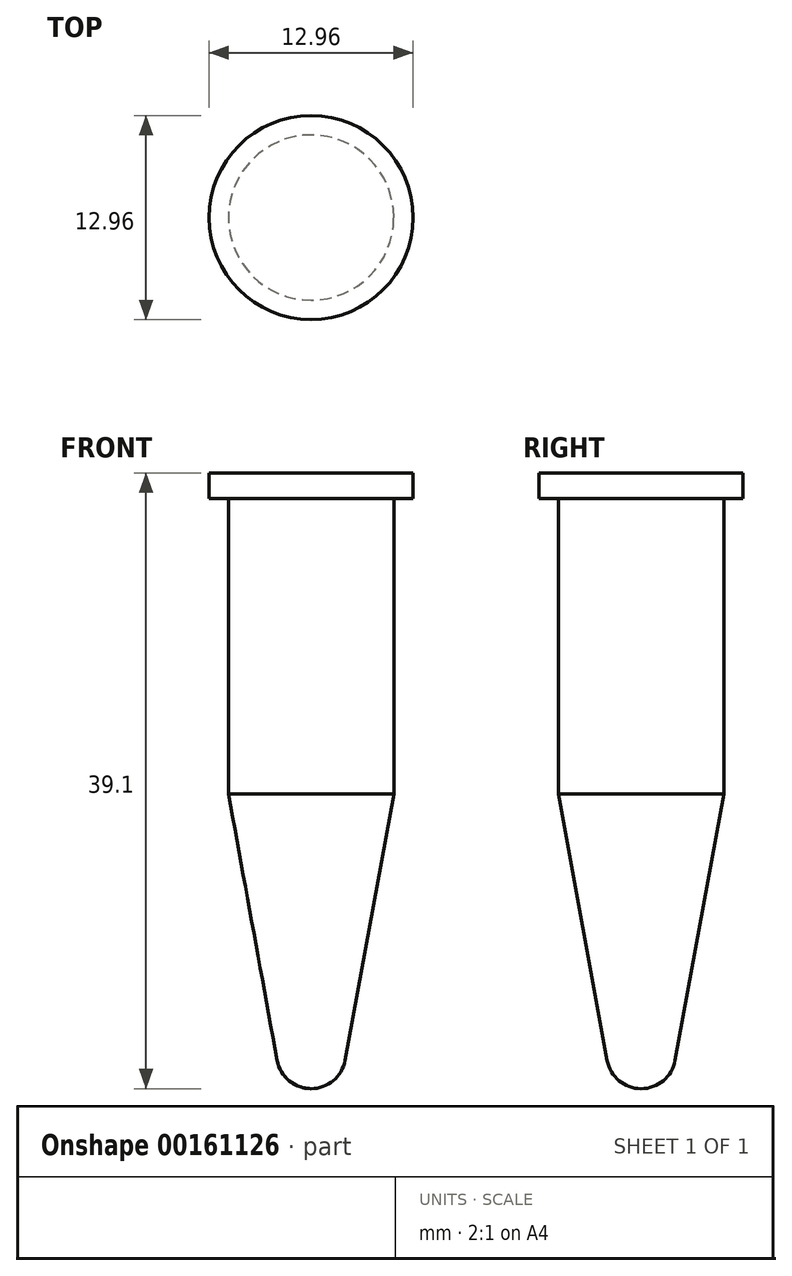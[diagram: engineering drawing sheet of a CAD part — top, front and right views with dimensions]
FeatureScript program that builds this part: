
annotation { "Feature Type Name" : "Feature", "Feature Type Description" : "" }
export const myFeature = defineFeature(function(context is Context, id is Id, definition is map)
    precondition{}
    {
        {
            var Q0;
            Q0=qCreatedBy(makeId("Front.planeOp"),FACE);
            var sketch = newSketch(context, id + "F0", { "sketchPlane" : qUnion([Q0])});
            skLineSegment(sketch, "E0", {"start": v(0, 0) * mm, "end": v(0, 39.1) * mm});
            skLineSegment(sketch, "E1", {"start": v(5.25, 37.5) * mm, "end": v(5.25, 18.72) * mm});
            skArc(sketch, "E2", {"start": v(0, 0) * mm, "mid": v(1.4, 0.5) * mm, "end": v(2.16, 1.8) * mm});
            skLineSegment(sketch, "E3", {"start": v(5.25, 18.72) * mm, "end": v(2.16, 1.8) * mm});
            skLineSegment(sketch, "E4", {"start": v(0, 0) * mm, "end": v(-7, 0) * mm, "construction": true});
            skLineSegment(sketch, "E5", {"start": v(5.25, 37.5) * mm, "end": v(6.48, 37.5) * mm});
            skLineSegment(sketch, "E6", {"start": v(6.48, 37.5) * mm, "end": v(6.48, 39.1) * mm});
            skLineSegment(sketch, "E7", {"start": v(6.48, 39.1) * mm, "end": v(0, 39.1) * mm});
            skSolve(sketch);
        }
        {
            var Q0;
            Q0=makeQuery(id+"F0.imprint","IMPRINT",FACE,{"disambiguationData":[TD([[makeQuery(id+"F0.imprint","IMPRINT",EDGE,{"derivedFrom":sQuery(id+"F0.wireOp",EDGE,"E0")}),-1.0]])]});
            var Q1;
            Q1=sQuery(id+"F0.wireOp",EDGE,"E0");
            revolve(context, id + "F1", {"entities" : qUnion([Q0]), "axis" : qUnion([Q1]), "revolveType" : RevolveType.FULL});
        }
    });
